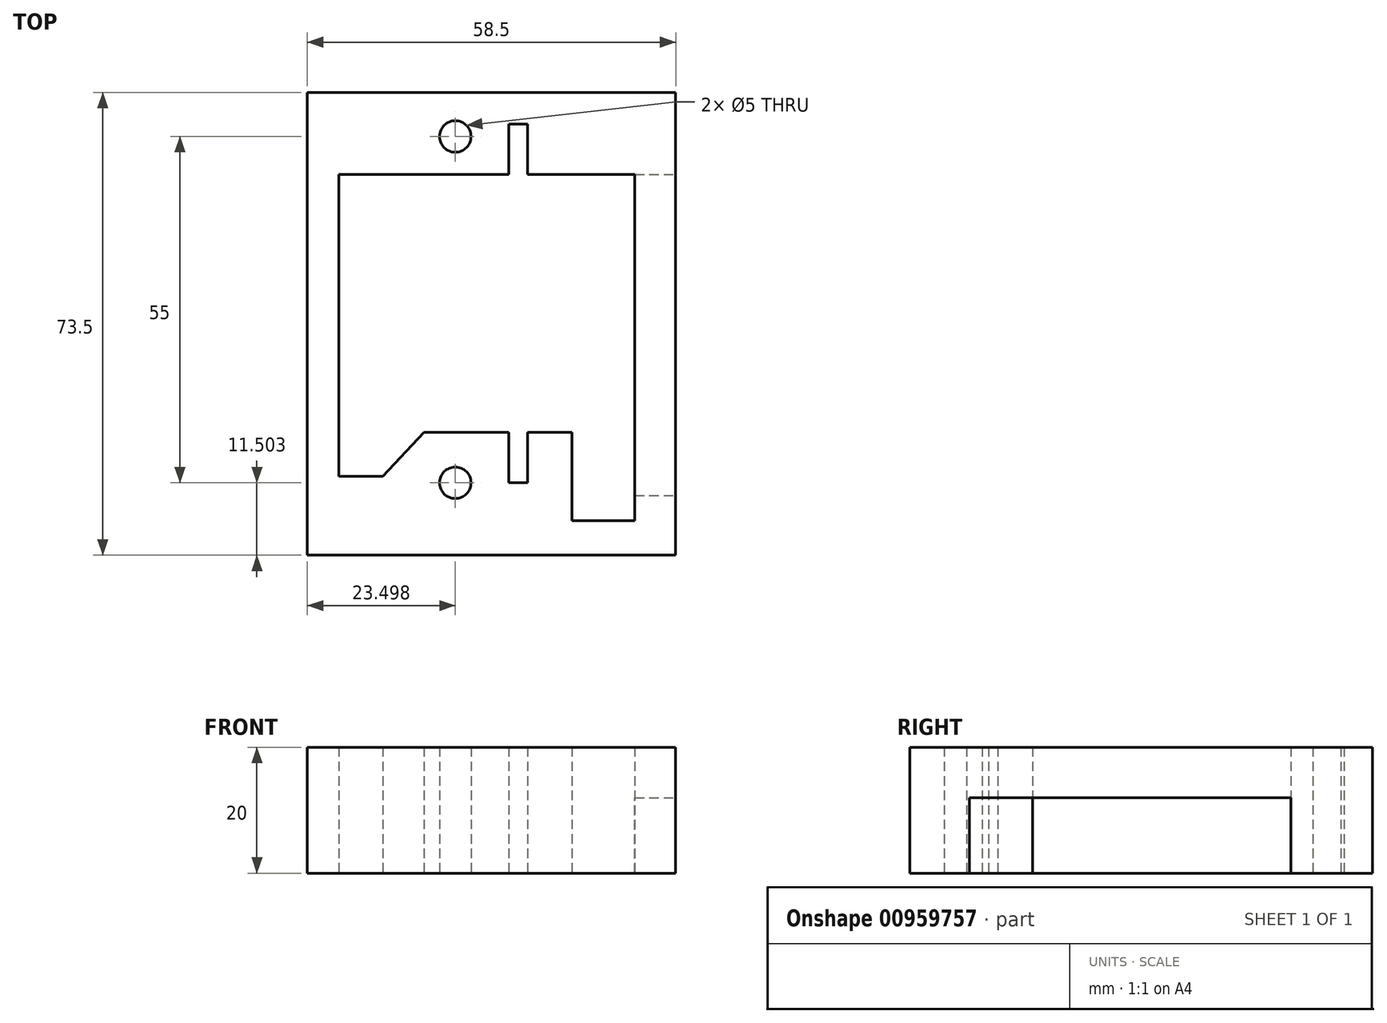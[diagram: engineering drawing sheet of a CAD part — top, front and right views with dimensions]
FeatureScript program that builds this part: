
annotation { "Feature Type Name" : "Feature", "Feature Type Description" : "" }
export const myFeature = defineFeature(function(context is Context, id is Id, definition is map)
    precondition{}
    {
        {
            var Q0;
            Q0=qCreatedBy(makeId("Top.planeOp"),FACE);
            var sketch = newSketch(context, id + "F0", { "sketchPlane" : qUnion([Q0])});
            skLineSegment(sketch, "E0.top", {"start": v(21.8, 21.77) * mm, "end": v(-15.2, 21.77) * mm});
            skLineSegment(sketch, "E1.top", {"start": v(21.8, -19.23) * mm, "end": v(-15.2, -19.23) * mm});
            skLineSegment(sketch, "E2", {"start": v(-15.2, 21.77) * mm, "end": v(11.8, 21.77) * mm});
            skLineSegment(sketch, "E3.bottom", {"start": v(11.8, 21.77) * mm, "end": v(14.8, 21.77) * mm});
            skLineSegment(sketch, "E3.top", {"start": v(11.8, 29.77) * mm, "end": v(14.8, 29.77) * mm});
            skLineSegment(sketch, "E3.left", {"start": v(11.8, 21.77) * mm, "end": v(11.8, 29.77) * mm});
            skLineSegment(sketch, "E3.right", {"start": v(14.8, 21.77) * mm, "end": v(14.8, 29.77) * mm});
            skLineSegment(sketch, "E4", {"start": v(-15.2, -19.23) * mm, "end": v(11.8, -19.23) * mm});
            skLineSegment(sketch, "E5.bottom", {"start": v(11.8, -19.23) * mm, "end": v(14.8, -19.23) * mm});
            skLineSegment(sketch, "E5.top", {"start": v(11.8, -27.23) * mm, "end": v(14.8, -27.23) * mm});
            skLineSegment(sketch, "E5.left", {"start": v(11.8, -19.23) * mm, "end": v(11.8, -27.23) * mm});
            skLineSegment(sketch, "E5.right", {"start": v(14.8, -19.23) * mm, "end": v(14.8, -27.23) * mm});
            skLineSegment(sketch, "E6.bottom", {"start": v(-15.2, -19.23) * mm, "end": v(-8.2, -19.23) * mm});
            skLineSegment(sketch, "E6.top", {"start": v(-15.2, -26.23) * mm, "end": v(-8.2, -26.23) * mm});
            skLineSegment(sketch, "E6.left", {"start": v(-15.2, -19.23) * mm, "end": v(-15.2, -26.23) * mm});
            skLineSegment(sketch, "E6.right", {"start": v(-8.2, -19.23) * mm, "end": v(-8.2, -26.23) * mm});
            skLineSegment(sketch, "E7", {"start": v(-15.2, 21.77) * mm, "end": v(-15.2, -19.23) * mm});
            skLineSegment(sketch, "E8", {"start": v(21.8, 21.77) * mm, "end": v(21.8, -19.23) * mm});
            skLineSegment(sketch, "E9", {"start": v(3.3, 21.77) * mm, "end": v(3.3, -19.23) * mm});
            skLineSegment(sketch, "E10.bottom", {"start": v(38.3, 41.27) * mm, "end": v(-31.7, 41.27) * mm});
            skLineSegment(sketch, "E10.top", {"start": v(38.3, -38.73) * mm, "end": v(-31.7, -38.73) * mm});
            skLineSegment(sketch, "E10.left", {"start": v(38.3, 41.27) * mm, "end": v(38.3, -38.73) * mm});
            skLineSegment(sketch, "E10.right", {"start": v(-31.7, 41.27) * mm, "end": v(-31.7, -38.73) * mm});
            skPoint(sketch, "E10.middle", {"position": v(3.3, 1.27) * mm});
            skLineSegment(sketch, "E11.bottom", {"start": v(21.8, 21.77) * mm, "end": v(31.8, 21.77) * mm});
            skLineSegment(sketch, "E11.top", {"start": v(21.8, -33.23) * mm, "end": v(31.8, -33.23) * mm});
            skLineSegment(sketch, "E11.left", {"start": v(21.8, 21.77) * mm, "end": v(21.8, -33.23) * mm});
            skLineSegment(sketch, "E11.right", {"start": v(31.8, 21.77) * mm, "end": v(31.8, -33.23) * mm});
            skLineSegment(sketch, "E12.bottom", {"start": v(38.3, -38.73) * mm, "end": v(-20.2, -38.73) * mm});
            skLineSegment(sketch, "E12.top", {"start": v(38.3, 34.77) * mm, "end": v(-20.2, 34.77) * mm});
            skLineSegment(sketch, "E12.left", {"start": v(38.3, -38.73) * mm, "end": v(38.3, 34.77) * mm});
            skLineSegment(sketch, "E12.right", {"start": v(-20.2, -38.73) * mm, "end": v(-20.2, 34.77) * mm});
            skCircle(sketch, "E13", {"center": v(3.3, -27.23) * mm, "radius": 2.5 * mm});
            skCircle(sketch, "E14", {"center": v(3.3, 27.77) * mm, "radius": 2.5 * mm});
            skLineSegment(sketch, "E15", {"start": v(-8.2, -26.23) * mm, "end": v(-1.7, -19.23) * mm});
            skSolve(sketch);
        }
        {
            var Q0;
            Q0=makeQuery(id+"F0.imprint","IMPRINT",FACE,{"disambiguationData":[TD([[makeQuery(id+"F0.imprint","IMPRINT",EDGE,{"derivedFrom":sQuery(id+"F0.wireOp",EDGE,"E3.top")}),1.0]])]});
            extrude(context, id + "F1", {"entities" : qUnion([Q0]), "depth" : 20 * mm, "offsetDistance" : 25.4 * mm});
        }
        {
            var Q0;
            Q0=makeQuery(id+"F1.opExtrude","SWEPT_FACE",FACE,{"disambiguationData":[OSD([sQuery(id+"F0.wireOp",EDGE,"E10.left")])]});
            var sketch = newSketch(context, id + "F2", { "sketchPlane" : qUnion([Q0])});
            skLineSegment(sketch, "E16.0.0", {"start": v(-38.73, 0) * mm, "end": v(34.77, 0) * mm});
            skLineSegment(sketch, "E16.0.1", {"start": v(34.77, 0) * mm, "end": v(34.77, 20) * mm});
            skLineSegment(sketch, "E16.0.2", {"start": v(34.77, 20) * mm, "end": v(-38.73, 20) * mm});
            skLineSegment(sketch, "E16.0.3", {"start": v(-38.73, 20) * mm, "end": v(-38.73, 0) * mm});
            skLineSegment(sketch, "E17.0", {"start": v(21.77, 20) * mm, "end": v(21.77, 0) * mm});
            skLineSegment(sketch, "E18.0", {"start": v(-33.23, 20) * mm, "end": v(-33.23, 0) * mm});
            skLineSegment(sketch, "E19.bottom", {"start": v(21.77, 20) * mm, "end": v(17.77, 20) * mm});
            skLineSegment(sketch, "E19.top", {"start": v(21.77, 12) * mm, "end": v(17.77, 12) * mm});
            skLineSegment(sketch, "E19.left", {"start": v(21.77, 20) * mm, "end": v(21.77, 12) * mm});
            skLineSegment(sketch, "E19.right", {"start": v(17.77, 20) * mm, "end": v(17.77, 12) * mm});
            skLineSegment(sketch, "E20.bottom", {"start": v(-33.23, 20) * mm, "end": v(-29.23, 20) * mm});
            skLineSegment(sketch, "E20.top", {"start": v(-33.23, 12) * mm, "end": v(-29.23, 12) * mm});
            skLineSegment(sketch, "E20.left", {"start": v(-33.23, 20) * mm, "end": v(-33.23, 12) * mm});
            skLineSegment(sketch, "E20.right", {"start": v(-29.23, 20) * mm, "end": v(-29.23, 12) * mm});
            skLineSegment(sketch, "E21.bottom", {"start": v(-29.23, 12) * mm, "end": v(17.77, 12) * mm});
            skLineSegment(sketch, "E21.top", {"start": v(-29.23, 0) * mm, "end": v(17.77, 0) * mm});
            skLineSegment(sketch, "E21.left", {"start": v(-29.23, 12) * mm, "end": v(-29.23, 0) * mm});
            skLineSegment(sketch, "E21.right", {"start": v(17.77, 12) * mm, "end": v(17.77, 0) * mm});
            skSolve(sketch);
        }
        {
            var Q0;
            Q0=makeQuery(id+"F2.imprint","IMPRINT",FACE,{"disambiguationData":[TD([[makeQuery(id+"F2.imprint","IMPRINT",EDGE,{"derivedFrom":sQuery(id+"F2.wireOp",EDGE,"E21.bottom")}),-1.0]])]});
            var Q1;
            {var subQ4=sQuery(id+"F2.wireOp",EDGE,"E19.top");Q1=makeQuery(id+"F2.imprint","IMPRINT",FACE,{"disambiguationData":[TD([[makeQuery(id+"F2.imprint","IMPRINT",EDGE,{"derivedFrom":subQ4}),1.0]])]});}
            extrude(context, id + "F3", {"entities" : qUnion([Q0, Q1]), "operationType" : NewBodyOperationType.REMOVE, "endBound" : BoundingType.UP_TO_NEXT, "oppositeDirection" : true, "depth" : 25.4 * mm, "offsetDistance" : 25.4 * mm});
        }
    });
